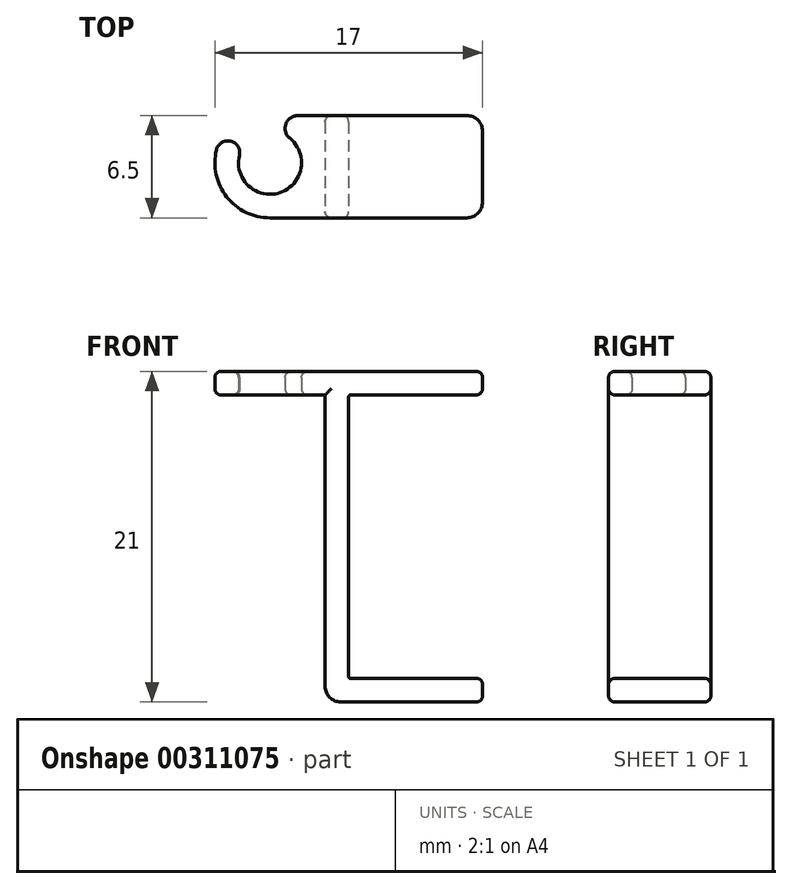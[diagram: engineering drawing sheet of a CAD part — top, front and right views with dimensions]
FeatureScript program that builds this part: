
annotation { "Feature Type Name" : "Feature", "Feature Type Description" : "" }
export const myFeature = defineFeature(function(context is Context, id is Id, definition is map)
    precondition{}
    {
        {
            var Q0;
            Q0=qCreatedBy(makeId("Top.planeOp"),FACE);
            var sketch = newSketch(context, id + "F0", { "sketchPlane" : qUnion([Q0])});
            skCircle(sketch, "E0", {"center": v(0, 0) * mm, "radius": 2 * mm, "construction": true});
            skLineSegment(sketch, "E1.bottom", {"start": v(13.5, 3) * mm, "end": v(1.77, 3) * mm});
            skLineSegment(sketch, "E1.top", {"start": v(13.5, -3.5) * mm, "end": v(1.77, -3.5) * mm});
            skLineSegment(sketch, "E1.left", {"start": v(13.5, 3) * mm, "end": v(13.5, -3.5) * mm});
            skLineSegment(sketch, "E1.right", {"start": v(1.77, 3) * mm, "end": v(1.77, -3.5) * mm, "construction": true});
            skPoint(sketch, "E1.middle", {"position": v(7.63, -0.25) * mm});
            skCircle(sketch, "E2", {"center": v(0, 0) * mm, "radius": 3.5 * mm, "construction": true});
            skLineSegment(sketch, "E3", {"start": v(1.77, -3.5) * mm, "end": v(0, -3.5) * mm});
            skArc(sketch, "E4", {"start": v(-3.4, 0.82) * mm, "mid": v(-2.75, -2.17) * mm, "end": v(0, -3.5) * mm});
            skArc(sketch, "E5", {"start": v(-1.94, 0.47) * mm, "mid": v(0.64, -1.9) * mm, "end": v(1.26, 1.55) * mm});
            skLineSegment(sketch, "E6", {"start": v(-1.94, 0.47) * mm, "end": v(-3.4, 0.82) * mm, "construction": true});
            skArc(sketch, "E7", {"start": v(-1.94, 0.47) * mm, "mid": v(-2.5, 1.37) * mm, "end": v(-3.4, 0.82) * mm});
            skArc(sketch, "E8", {"start": v(1.77, 3) * mm, "mid": v(1, 2.46) * mm, "end": v(1.26, 1.55) * mm});
            skSolve(sketch);
        }
        {
            var Q0;
            Q0=makeQuery(id+"F0.imprint","IMPRINT",FACE,{"disambiguationData":[TD([[makeQuery(id+"F0.imprint","IMPRINT",EDGE,{"derivedFrom":sQuery(id+"F0.wireOp",EDGE,"E1.bottom")}),1.0]])]});
            extrude(context, id + "F1", {"entities" : qUnion([Q0]), "depth" : 1.5 * mm});
        }
        {
            var Q0;
            Q0=makeQuery(id+"F1.opExtrude","SWEPT_FACE",FACE,{"disambiguationData":[OSD([sQuery(id+"F0.wireOp",EDGE,"E1.top"),sQuery(id+"F0.wireOp",EDGE,"E3")])]});
            var sketch = newSketch(context, id + "F2", { "sketchPlane" : qUnion([Q0])});
            skLineSegment(sketch, "E9.bottom", {"start": v(13.5, 0) * mm, "end": v(5, 0) * mm, "construction": true});
            skLineSegment(sketch, "E9.top", {"start": v(13.5, -18) * mm, "end": v(5, -18) * mm, "construction": true});
            skLineSegment(sketch, "E9.left", {"start": v(13.5, 0) * mm, "end": v(13.5, -18) * mm, "construction": true});
            skLineSegment(sketch, "E9.right", {"start": v(5, 0) * mm, "end": v(5, -18) * mm, "construction": true});
            skLineSegment(sketch, "E10", {"start": v(3.5, 0) * mm, "end": v(3.5, -19.5) * mm});
            skLineSegment(sketch, "E11", {"start": v(3.5, -19.5) * mm, "end": v(13.5, -19.5) * mm});
            skLineSegment(sketch, "E12", {"start": v(13.5, -19.5) * mm, "end": v(13.5, -18) * mm});
            skLineSegment(sketch, "E13", {"start": v(5, -18) * mm, "end": v(3.5, -18) * mm, "construction": true});
            skLineSegment(sketch, "E14", {"start": v(13.5, 0) * mm, "end": v(5, 0) * mm});
            skLineSegment(sketch, "E15", {"start": v(5, 0) * mm, "end": v(5, -18) * mm});
            skLineSegment(sketch, "E16", {"start": v(5, -18) * mm, "end": v(13.5, -18) * mm});
            skSolve(sketch);
        }
        {
            var Q0;
            {var subQ1=sQuery(id+"F2.wireOp",EDGE,"E10");Q0=makeQuery(id+"F2.imprint","IMPRINT",FACE,{"disambiguationData":[TD([[makeQuery(id+"F2.imprint","IMPRINT",EDGE,{"derivedFrom":subQ1}),1.0]])]});}
            var Q1;
            Q1=makeQuery(id+"F1.opExtrude","SWEPT_FACE",FACE,{"disambiguationData":[OSD([sQuery(id+"F0.wireOp",EDGE,"E1.bottom")])]});
            extrude(context, id + "F3", {"entities" : qUnion([Q0]), "operationType" : NewBodyOperationType.ADD, "endBound" : BoundingType.UP_TO_SURFACE, "oppositeDirection" : true, "endBoundEntityFace" : qUnion([Q1]), "depth" : 25 * mm});
        }
        {
            var Q0;
            Q0=makeQuery(id+"F3.opExtrude","SWEPT_EDGE",EDGE,{"disambiguationData":[OSD([sQuery(id+"F0.wireOp",EDGE,"E1.top"),sQuery(id+"F0.wireOp",EDGE,"E3"),sQuery(id+"F2.wireOp",EDGE,"E14"),sQuery(id+"F2.wireOp",EDGE,"E15")])]});
            var Q1;
            Q1=makeQuery(id+"F3.opExtrude","SWEPT_EDGE",EDGE,{"disambiguationData":[OSD([sQuery(id+"F2.wireOp",EDGE,"E15"),sQuery(id+"F2.wireOp",EDGE,"E16")])]});
            fillet(context, id + "F4", {"entities" : qUnion([Q0, Q1]), "radius" : 0.1 * mm, "tangentPropagation" : true, "allowEdgeOverflow" : false});
        }
        {
            var Q0;
            Q0=makeQuery(id+"F3.opExtrude","SWEPT_EDGE",EDGE,{"disambiguationData":[OSD([sQuery(id+"F0.wireOp",EDGE,"E1.top"),sQuery(id+"F0.wireOp",EDGE,"E3"),sQuery(id+"F2.wireOp",EDGE,"E10")])]});
            var Q1;
            Q1=makeQuery(id+"F3.opExtrude","SWEPT_EDGE",EDGE,{"disambiguationData":[OSD([sQuery(id+"F2.wireOp",EDGE,"E10"),sQuery(id+"F2.wireOp",EDGE,"E11")])]});
            fillet(context, id + "F5", {"entities" : qUnion([Q0, Q1]), "radius" : 1 * mm, "tangentPropagation" : true, "allowEdgeOverflow" : false});
        }
        {
            var Q0;
            Q0=makeQuery(id+"F3.opExtrude","CAP_EDGE",EDGE,{"disambiguationData":[OSD([sQuery(id+"F2.wireOp",EDGE,"E12")])],"isStart":true});
            var Q1;
            Q1=makeQuery(id+"F3.opExtrude","CAP_EDGE",EDGE,{"disambiguationData":[OSD([sQuery(id+"F2.wireOp",EDGE,"E12")])],"isStart":false});
            var Q2;
            Q2=makeQuery(id+"F1.opExtrude","SWEPT_EDGE",EDGE,{"disambiguationData":[OSD([sQuery(id+"F0.wireOp",EDGE,"E1.top"),sQuery(id+"F0.wireOp",EDGE,"E1.left")])]});
            var Q3;
            Q3=makeQuery(id+"F1.opExtrude","SWEPT_EDGE",EDGE,{"disambiguationData":[OSD([sQuery(id+"F0.wireOp",EDGE,"E1.bottom"),sQuery(id+"F0.wireOp",EDGE,"E1.left")])]});
            fillet(context, id + "F6", {"entities" : qUnion([Q0, Q1, Q2, Q3]), "radius" : 1 * mm, "tangentPropagation" : true, "allowEdgeOverflow" : false});
        }
        {
            var Q0;
            Q0=makeQuery(id+"F1.opExtrude","CAP_FACE",FACE,{"disambiguationData":[OSD([sQuery(id+"F0.wireOp",EDGE,"E1.bottom"),sQuery(id+"F0.wireOp",EDGE,"E1.top"),sQuery(id+"F0.wireOp",EDGE,"E1.left"),sQuery(id+"F0.wireOp",EDGE,"E3"),sQuery(id+"F0.wireOp",EDGE,"E4"),sQuery(id+"F0.wireOp",EDGE,"E5"),sQuery(id+"F0.wireOp",EDGE,"E7"),sQuery(id+"F0.wireOp",EDGE,"E8")])],"isStart":false});
            var Q1;
            {var subQ0=sQuery(id+"F0.wireOp",EDGE,"E3");var subQ1=sQuery(id+"F0.wireOp",EDGE,"E1.top");Q1=makeQuery(id+"F3.boolean.opBoolean","MERGE",FACE,{"derivedFrom":[makeQuery(id+"F1.opExtrude","SWEPT_FACE",FACE,{"disambiguationData":[OSD([subQ1,subQ0])]}),makeQuery(id+"F3.opExtrude","CAP_FACE",FACE,{"disambiguationData":[OSD([subQ1,subQ0,sQuery(id+"F2.wireOp",EDGE,"E10"),sQuery(id+"F2.wireOp",EDGE,"E11"),sQuery(id+"F2.wireOp",EDGE,"E12"),sQuery(id+"F2.wireOp",EDGE,"E15"),sQuery(id+"F2.wireOp",EDGE,"E16")])],"isStart":true})]});}
            fillet(context, id + "F7", {"entities" : qUnion([Q0, Q1]), "radius" : 0.4 * mm, "tangentPropagation" : true, "allowEdgeOverflow" : false});
        }
    });
